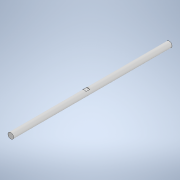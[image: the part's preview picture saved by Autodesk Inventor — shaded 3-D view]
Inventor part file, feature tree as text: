
AUTODESK INVENTOR PART (.ipt)
format: ipt  version: 2021 (Build 250183000, 183)  size: 102,400 bytes
history: native  units: in
note: dims shown in document units (in); Inventor stores cm internally (conversion verified against a paired STEP export)
features: extrude x2, sketch x2, other x1, plane x1
ambient origin geometry x8: Origin, YZ Plane, XZ Plane, XY Plane, X Axis, Y Axis, Z Axis, Center Point
bodies: Body1 (feature_tree)
feature tree (6):
  other  "Sólido1"
  extrude  "Extrusión1"  Depth=16.5354in TaperAngle=0.0deg
  plane  "Plano de trabajo1"
  extrude  "Extrusión4"  Depth=0.3937in
  sketch  "Boceto1"  dims[d0=0.5906in d1=16.5354in d2=0.0in]
  sketch  "Boceto5"  dims[d9=0.1969in d10=0.5906in d11=0.0591in d12=0.3937in d13=0.0in]
